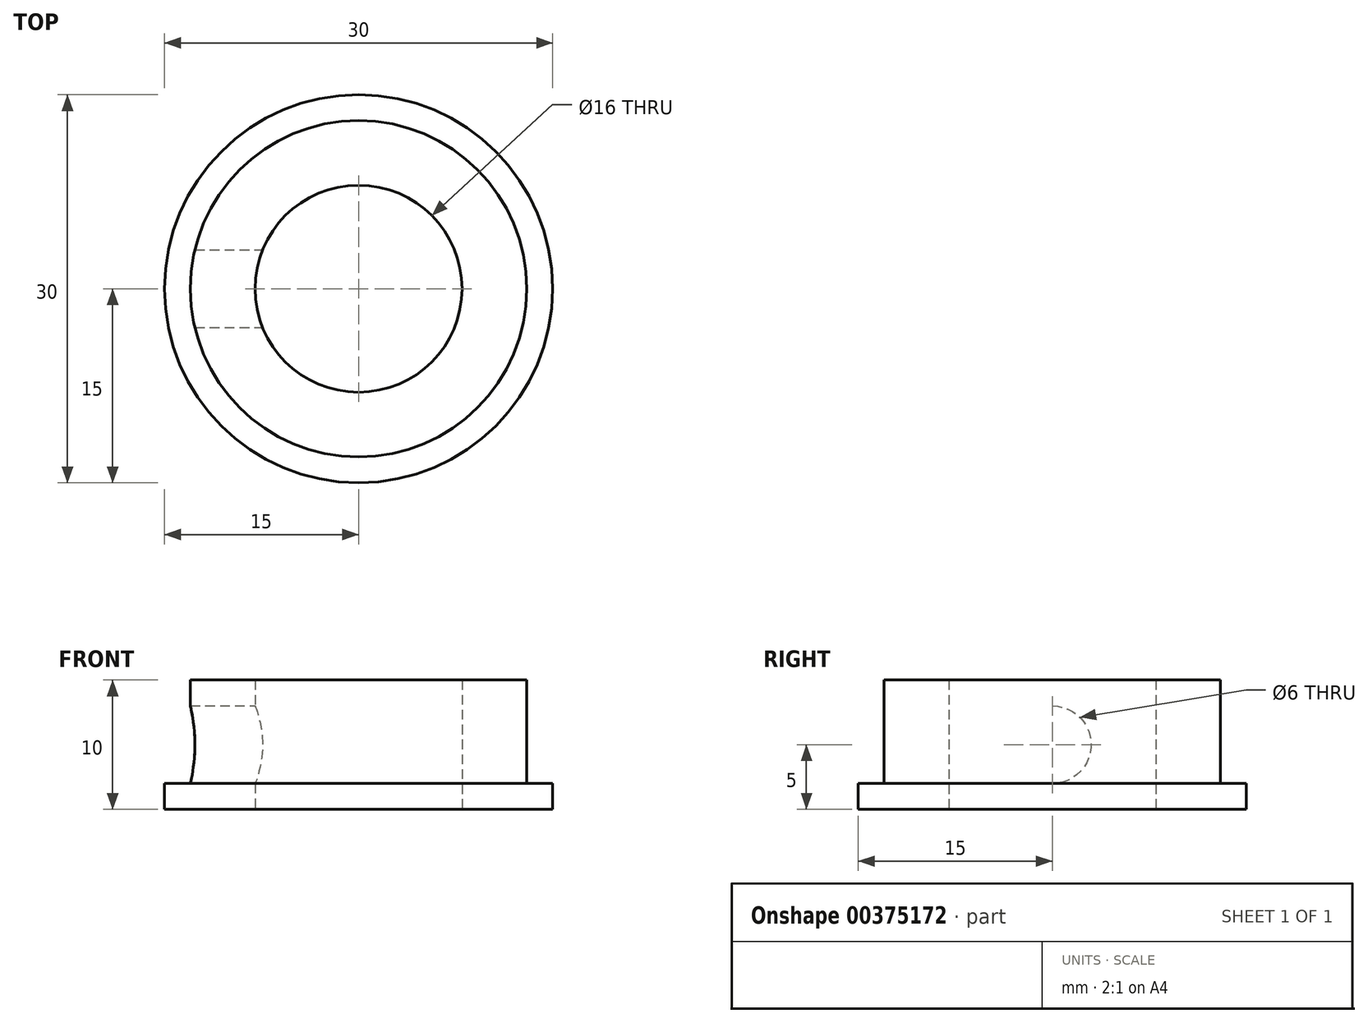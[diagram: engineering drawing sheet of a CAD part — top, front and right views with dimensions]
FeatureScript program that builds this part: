
annotation { "Feature Type Name" : "Feature", "Feature Type Description" : "" }
export const myFeature = defineFeature(function(context is Context, id is Id, definition is map)
    precondition{}
    {
        {
            var Q0;
            Q0=qCreatedBy(makeId("Top.planeOp"),FACE);
            var sketch = newSketch(context, id + "F0", { "sketchPlane" : qUnion([Q0])});
            skCircle(sketch, "E0", {"center": v(0, 0) * mm, "radius": 15 * mm});
            skCircle(sketch, "E1", {"center": v(0, 0) * mm, "radius": 8 * mm});
            skSolve(sketch);
        }
        {
            var Q0;
            Q0=makeQuery(id+"F0.imprint","IMPRINT",FACE,{"disambiguationData":[TD([[makeQuery(id+"F0.imprint","IMPRINT",EDGE,{"derivedFrom":sQuery(id+"F0.wireOp",EDGE,"E0")}),1.0]])]});
            extrude(context, id + "F1", {"entities" : qUnion([Q0]), "depth" : 2 * mm});
        }
        {
            var Q0;
            Q0=makeQuery(id+"F1.opExtrude","CAP_FACE",FACE,{"disambiguationData":[OSD([sQuery(id+"F0.wireOp",EDGE,"E0"),sQuery(id+"F0.wireOp",EDGE,"E1")])],"isStart":false});
            var sketch = newSketch(context, id + "F2", { "sketchPlane" : qUnion([Q0])});
            skCircle(sketch, "E2", {"center": v(0, 0) * mm, "radius": 8 * mm});
            skCircle(sketch, "E3", {"center": v(0, 0) * mm, "radius": 13 * mm});
            skSolve(sketch);
        }
        {
            var Q0;
            Q0=makeQuery(id+"F2.imprint","IMPRINT",FACE,{"disambiguationData":[TD([[makeQuery(id+"F2.imprint","IMPRINT",EDGE,{"derivedFrom":sQuery(id+"F2.wireOp",EDGE,"E2")}),-1.0]])]});
            extrude(context, id + "F3", {"entities" : qUnion([Q0]), "operationType" : NewBodyOperationType.ADD, "depth" : 8 * mm});
        }
        {
            var Q0;
            Q0=qCreatedBy(makeId("Right.planeOp"),FACE);
            var sketch = newSketch(context, id + "F4", { "sketchPlane" : qUnion([Q0])});
            skPoint(sketch, "E4", {"position": v(0, 5) * mm});
            skSolve(sketch);
        }
        {
            var Q0;
            Q0=sQuery(id+"F4.wireOp",VERTEX,"E4");
            var Q1;
            Q1=makeQuery(id+"F1.opExtrude","SWEPT_BODY",BODY,{"disambiguationData":[OSD([sQuery(id+"F0.wireOp",EDGE,"E0"),sQuery(id+"F0.wireOp",EDGE,"E1")])]});
            hole(context, id + "F5", {"style" : HoleStyle.SIMPLE, "endStyle" : HoleEndStyle.BLIND, "holeDiameter" : 6 * mm, "holeDepth" : 25 * mm, "isTappedThrough" : true, "tappedDepth" : 12 * mm, "tapClearance" : 3, "locations" : qUnion([Q0]), "scope" : qUnion([Q1])});
        }
    });
